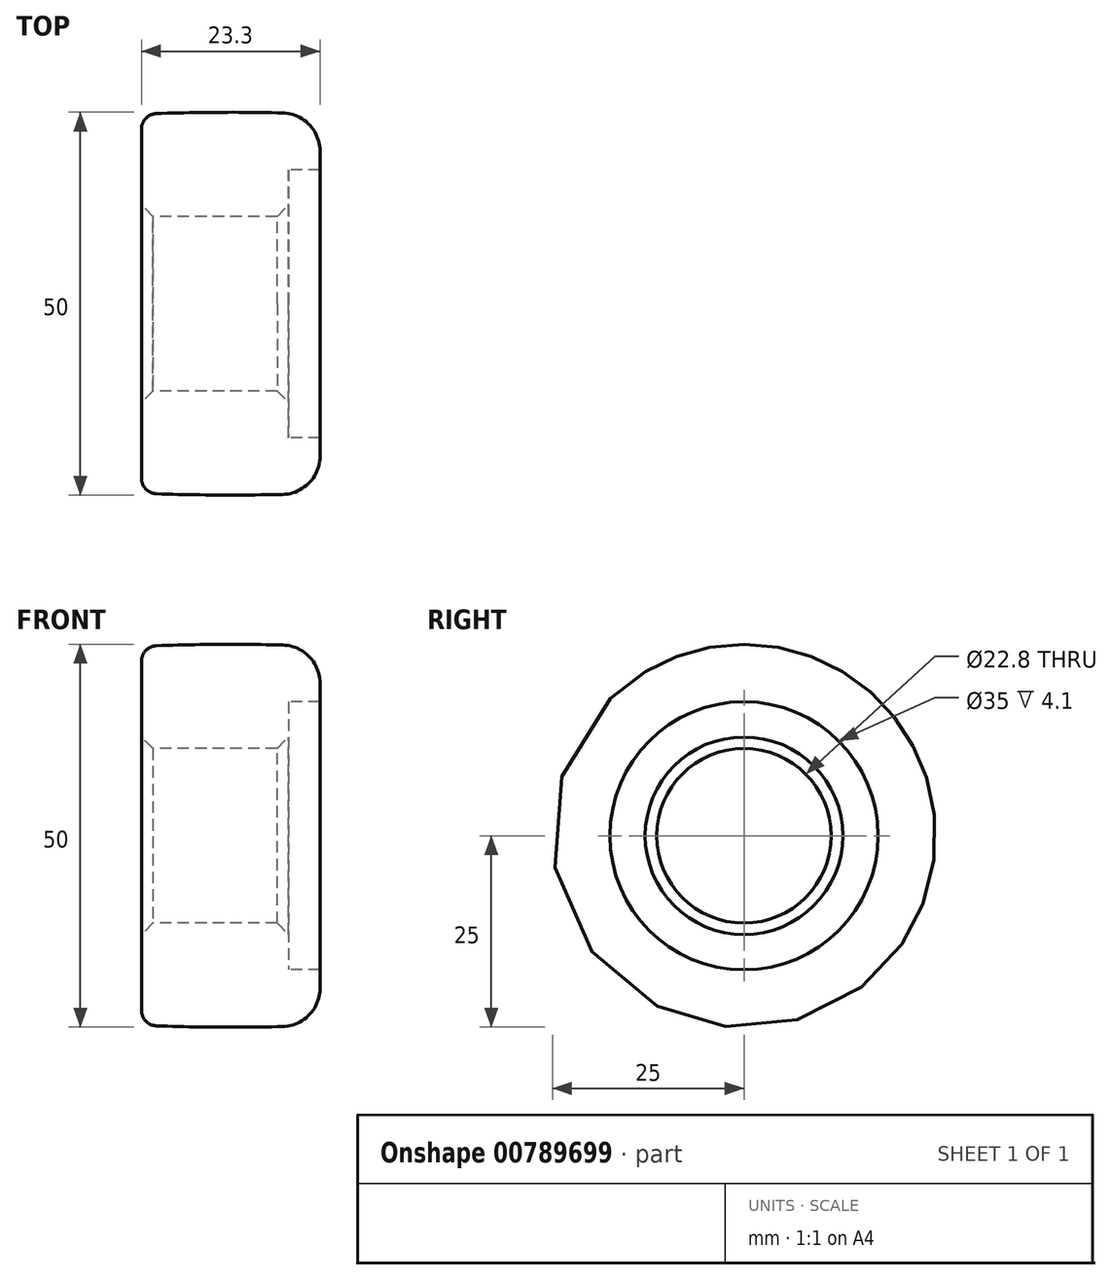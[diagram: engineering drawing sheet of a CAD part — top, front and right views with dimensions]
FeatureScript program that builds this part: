
annotation { "Feature Type Name" : "Feature", "Feature Type Description" : "" }
export const myFeature = defineFeature(function(context is Context, id is Id, definition is map)
    precondition{}
    {
        {
            var Q0;
            Q0=qCreatedBy(makeId("Front.planeOp"),FACE);
            var sketch = newSketch(context, id + "F0", { "sketchPlane" : qUnion([Q0])});
            skLineSegment(sketch, "E0", {"start": v(1.22, 0) * mm, "end": v(33.82, 0) * mm, "construction": true});
            skLineSegment(sketch, "E1", {"start": v(0, 11.4) * mm, "end": v(0, 22.83) * mm});
            skLineSegment(sketch, "E2", {"start": v(23.3, 19.92) * mm, "end": v(23.3, 17.5) * mm});
            skLineSegment(sketch, "E3", {"start": v(23.3, 17.5) * mm, "end": v(19.2, 17.5) * mm});
            skLineSegment(sketch, "E4", {"start": v(19.2, 17.5) * mm, "end": v(19.2, 11.4) * mm});
            skLineSegment(sketch, "E5", {"start": v(19.2, 11.4) * mm, "end": v(0, 11.4) * mm});
            skLineSegment(sketch, "E6", {"start": v(11.65, 18.86) * mm, "end": v(11.65, 29.37) * mm, "construction": true});
            skPoint(sketch, "E6.startSnap0", {"position": v(11.65, 23.78) * mm});
            skPoint(sketch, "E7", {"position": v(11.65, 25) * mm});
            skArc(sketch, "E8", {"start": v(18.42, 24.92) * mm, "mid": v(10.18, 25) * mm, "end": v(1.93, 24.83) * mm});
            skPoint(sketch, "E9.visualSharp", {"position": v(23.3, 24.75) * mm});
            skArc(sketch, "E9.filletArc", {"start": v(23.3, 19.92) * mm, "mid": v(21.88, 23.4) * mm, "end": v(18.42, 24.92) * mm});
            skPoint(sketch, "E10.visualSharp", {"position": v(0, 24.75) * mm});
            skArc(sketch, "E10.filletArc", {"start": v(1.93, 24.83) * mm, "mid": v(0.56, 24.22) * mm, "end": v(0, 22.83) * mm});
            skSolve(sketch);
        }
        {
            var Q0;
            Q0=makeQuery(id+"F0.imprint","IMPRINT",FACE,{"disambiguationData":[TD([[makeQuery(id+"F0.imprint","IMPRINT",EDGE,{"derivedFrom":sQuery(id+"F0.wireOp",EDGE,"E1")}),-1.0]])]});
            var Q1;
            Q1=sQuery(id+"F0.wireOp",EDGE,"E0");
            revolve(context, id + "F1", {"surfaceOperationType" : NewSurfaceOperationType.NEW, "entities" : qUnion([Q0]), "axis" : qUnion([Q1]), "revolveType" : RevolveType.FULL});
        }
        {
            var Q0;
            Q0=makeQuery(id+"F1.opRevolve","SWEPT_EDGE",EDGE,{"disambiguationData":[OSD([sQuery(id+"F0.wireOp",EDGE,"E1"),sQuery(id+"F0.wireOp",EDGE,"E5")])]});
            var Q1;
            Q1=makeQuery(id+"F1.opRevolve","SWEPT_EDGE",EDGE,{"disambiguationData":[OSD([sQuery(id+"F0.wireOp",EDGE,"E4"),sQuery(id+"F0.wireOp",EDGE,"E5")])]});
            chamfer(context, id + "F2", {"entities" : qUnion([Q0, Q1]), "width" : 1.5 * mm, "tangentPropagation" : true});
        }
    });
